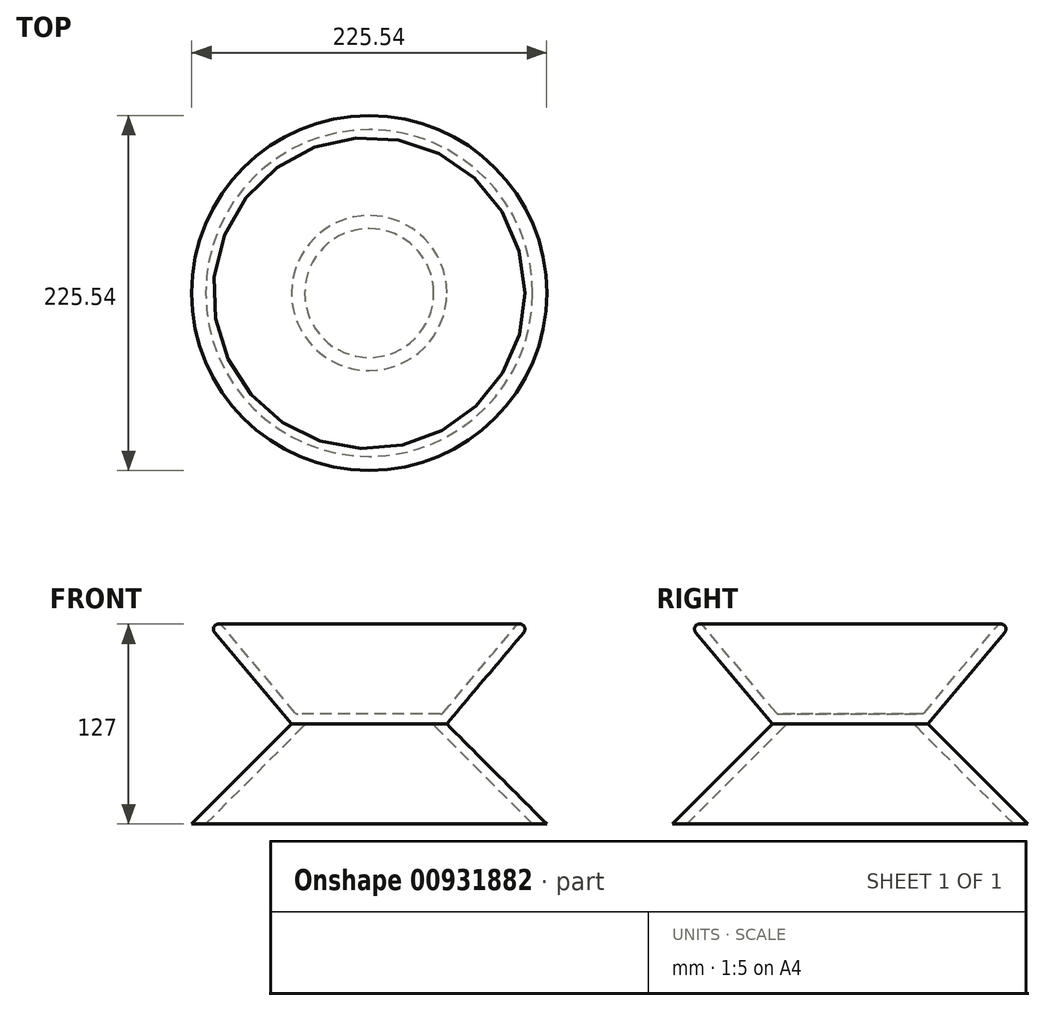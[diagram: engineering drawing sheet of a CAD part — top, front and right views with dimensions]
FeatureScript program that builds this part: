
annotation { "Feature Type Name" : "Feature", "Feature Type Description" : "" }
export const myFeature = defineFeature(function(context is Context, id is Id, definition is map)
    precondition{}
    {
        {
            var Q0;
            Q0=qCreatedBy(makeId("Top.planeOp"),FACE);
            var sketch = newSketch(context, id + "F0", { "sketchPlane" : qUnion([Q0])});
            skCircle(sketch, "E0", {"center": v(0, 0) * mm, "radius": 49.27 * mm});
            skSolve(sketch);
        }
        {
            var Q0;
            Q0=qSketchRegion(id+"F0",true);
            extrude(context, id + "F1", {"entities" : qUnion([Q0]), "depth" : 63.5 * mm, "offsetDistance" : 25.4 * mm, "hasDraft" : true, "draftAngle" : 40 * degree});
        }
        {
            var Q0;
            Q0=makeQuery(id+"F1.opExtrude","CAP_FACE",FACE,{"disambiguationData":[OSD([sQuery(id+"F0.wireOp",EDGE,"E0")])],"isStart":false});
            shell(context, id + "F2", {"entities" : qUnion([Q0]), "thickness" : 6.35 * mm});
        }
        {
            var Q0;
            Q0=makeQuery(id+"F1.opExtrude","CAP_EDGE",EDGE,{"disambiguationData":[OSD([sQuery(id+"F0.wireOp",EDGE,"E0")])],"isStart":false});
            var Q1;
            {var subQ0=sQuery(id+"F0.wireOp",EDGE,"E0");Q1=makeQuery(id+"F2.opShell","OFFSET_EDGE",EDGE,{"disambiguationData":[OSD([subQ0]),TDD([makeQuery(id+"F1.opExtrude","CAP_EDGE",EDGE,{"disambiguationData":[OSD([subQ0])],"isStart":false})])]});}
            fillet(context, id + "F3", {"entities" : qUnion([Q0, Q1]), "radius" : 3.17 * mm, "tangentPropagation" : true, "allowEdgeOverflow" : false});
        }
        {
            var Q0;
            Q0=makeQuery(id+"F1.opExtrude","CAP_FACE",FACE,{"disambiguationData":[OSD([sQuery(id+"F0.wireOp",EDGE,"E0")])],"isStart":true});
            extrude(context, id + "F4", {"entities" : qUnion([Q0]), "operationType" : NewBodyOperationType.ADD, "depth" : 63.5 * mm, "offsetDistance" : 25.4 * mm, "hasDraft" : true, "draftAngle" : 45 * degree});
        }
        {
            var Q0;
            Q0=makeQuery(id+"F4.opExtrude","CAP_FACE",FACE,{"disambiguationData":[OSD([sQuery(id+"F0.wireOp",EDGE,"E0")])],"isStart":false});
            shell(context, id + "F5", {"entities" : qUnion([Q0]), "thickness" : 6.35 * mm});
        }
        {
            var Q0;
            {var subQ0=sQuery(id+"F0.wireOp",EDGE,"E0");Q0=makeQuery(id+"F2.opShell","OFFSET_EDGE",EDGE,{"disambiguationData":[OSD([subQ0]),TDD([makeQuery(id+"F1.opExtrude","CAP_EDGE",EDGE,{"disambiguationData":[OSD([subQ0])],"isStart":true})])]});}
            fillet(context, id + "F6", {"entities" : qUnion([Q0]), "radius" : 2.3 * mm, "tangentPropagation" : true, "allowEdgeOverflow" : false});
        }
        {
            var Q0;
            {var subQ0=sQuery(id+"F0.wireOp",EDGE,"E0");Q0=makeQuery(id+"F5.opShell","OFFSET_EDGE",EDGE,{"disambiguationData":[OSD([subQ0]),TDD([makeQuery(id+"F4.boolean.opBoolean","MERGE",EDGE,{"derivedFrom":[makeQuery(id+"F1.opExtrude","CAP_EDGE",EDGE,{"disambiguationData":[OSD([subQ0])],"isStart":true}),makeQuery(id+"F4.opExtrude","CAP_EDGE",EDGE,{"disambiguationData":[OSD([subQ0])],"isStart":true})]})])]});}
            fillet(context, id + "F7", {"entities" : qUnion([Q0]), "radius" : 2.3 * mm, "tangentPropagation" : true, "allowEdgeOverflow" : false});
        }
    });
